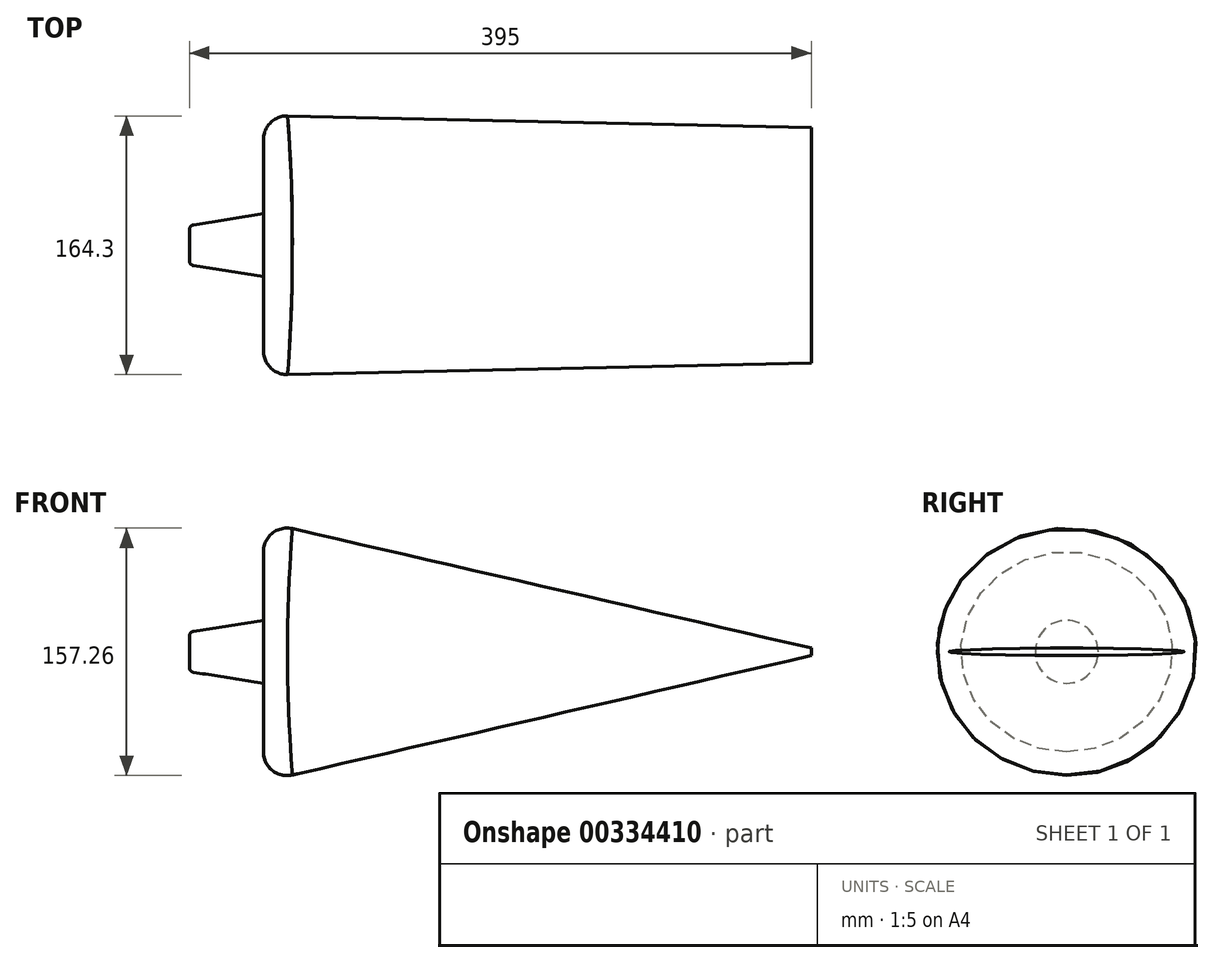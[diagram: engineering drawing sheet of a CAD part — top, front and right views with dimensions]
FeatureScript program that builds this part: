
annotation { "Feature Type Name" : "Feature", "Feature Type Description" : "" }
export const myFeature = defineFeature(function(context is Context, id is Id, definition is map)
    precondition{}
    {
        {
            var Q0;
            Q0=qCreatedBy(makeId("Right.planeOp"),FACE);
            cPlane(context, id + "F0", {"entities" : qUnion([Q0]), "cplaneType" : CPlaneType.OFFSET, "offset" : 348 * mm, "width" : 150 * mm, "height" : 150 * mm});
        }
        {
            var Q0;
            Q0=qCreatedBy(id+"F0.planeOp",FACE);
            var sketch = newSketch(context, id + "F1", { "sketchPlane" : qUnion([Q0])});
            skEllipse(sketch, "E0", {"center": v(0, 0) * mm, "majorRadius": 74.83 * mm, "minorRadius": 2.35 * mm, "majorAxis": v(1, 0)});
            skSolve(sketch);
        }
        {
            var Q0;
            Q0=qCreatedBy(makeId("Right.planeOp"),FACE);
            var sketch = newSketch(context, id + "F2", { "sketchPlane" : qUnion([Q0])});
            skCircle(sketch, "E1", {"center": v(0, 0) * mm, "radius": 82.48 * mm});
            skSolve(sketch);
        }
        {
            var Q0;
            Q0=makeQuery(id+"F2.imprint","IMPRINT",FACE,{"disambiguationData":[TD([[makeQuery(id+"F2.imprint","IMPRINT",EDGE,{"derivedFrom":sQuery(id+"F2.wireOp",EDGE,"E1")}),1.0]])]});
            var Q1;
            Q1=makeQuery(id+"F1.imprint","IMPRINT",FACE,{"disambiguationData":[TD([[makeQuery(id+"F1.imprint","IMPRINT",EDGE,{"derivedFrom":sQuery(id+"F1.wireOp",EDGE,"E0")}),1.0]])]});
            loft(context, id + "F3", {"sheetProfilesArray" : [{ "sheetProfileEntities" : qUnion([Q0]) }, { "sheetProfileEntities" : qUnion([Q1]) }]});
        }
        {
            var Q0;
            Q0=makeQuery(id+"F3.opLoft","CAP_FACE",FACE,{"disambiguationData":[OSD([makeQuery(id+"F2.imprint","IMPRINT",FACE,{"disambiguationData":[TD([[makeQuery(id+"F2.imprint","IMPRINT",EDGE,{"derivedFrom":sQuery(id+"F2.wireOp",EDGE,"E1")}),1.0]])]})])],"isStart":true});
            fillet(context, id + "F4", {"entities" : qUnion([Q0]), "radius" : 15 * mm, "tangentPropagation" : true, "allowEdgeOverflow" : false});
        }
        {
            var Q0;
            Q0=makeQuery(id+"F3.opLoft","CAP_FACE",FACE,{"disambiguationData":[OSD([makeQuery(id+"F2.imprint","IMPRINT",FACE,{"disambiguationData":[TD([[makeQuery(id+"F2.imprint","IMPRINT",EDGE,{"derivedFrom":sQuery(id+"F2.wireOp",EDGE,"E1")}),1.0]])]})])],"isStart":true});
            var sketch = newSketch(context, id + "F5", { "sketchPlane" : qUnion([Q0])});
            skCircle(sketch, "E2", {"center": v(0, 0) * mm, "radius": 20 * mm});
            skSolve(sketch);
        }
        {
            var Q0;
            Q0 = qSketchRegion(id + "F5", true);
            extrude(context, id + "F6", {"entities" : qUnion([Q0]), "operationType" : NewBodyOperationType.ADD, "depth" : 47 * mm, "hasDraft" : true, "draftAngle" : 9 * degree, "draftPullDirection" : true});
        }
        {
            var Q0;
            Q0=makeQuery(id+"F6.opExtrude","CAP_FACE",FACE,{"disambiguationData":[OSD([sQuery(id+"F5.wireOp",EDGE,"E2")])],"isStart":false});
            fillet(context, id + "F7", {"entities" : qUnion([Q0]), "radius" : 3 * mm, "tangentPropagation" : true, "allowEdgeOverflow" : false});
        }
    });
